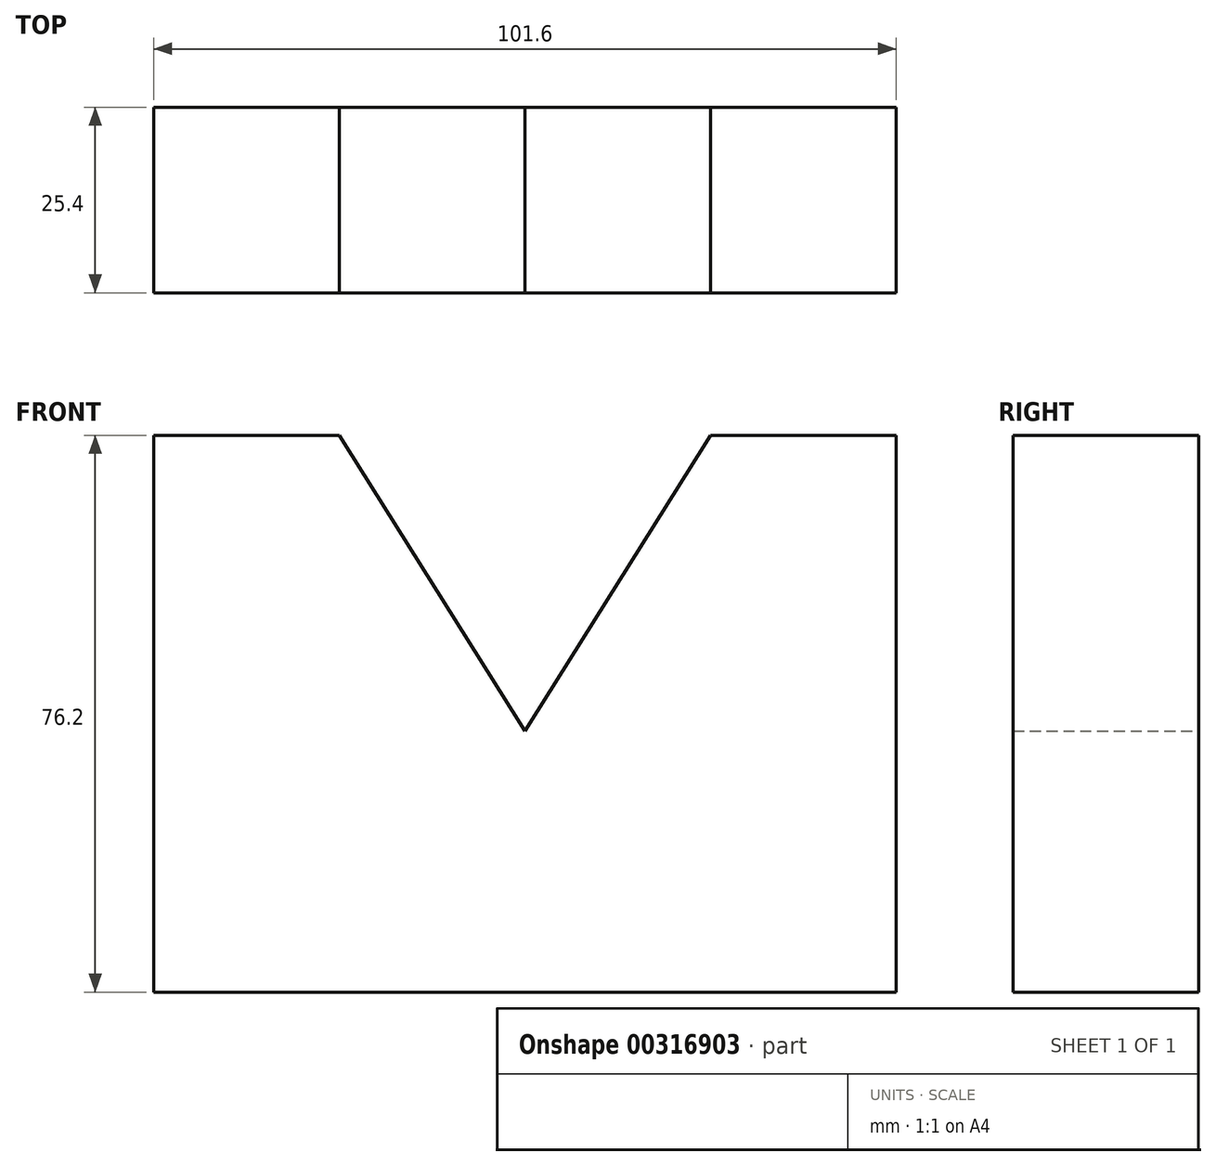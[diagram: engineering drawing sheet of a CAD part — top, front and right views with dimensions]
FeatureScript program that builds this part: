
annotation { "Feature Type Name" : "Feature", "Feature Type Description" : "" }
export const myFeature = defineFeature(function(context is Context, id is Id, definition is map)
    precondition{}
    {
        {
            var Q0;
            Q0=qCreatedBy(makeId("Front.planeOp"),FACE);
            var sketch = newSketch(context, id + "F0", { "sketchPlane" : qUnion([Q0])});
            skLineSegment(sketch, "E0", {"start": v(-47.04, 43.55) * mm, "end": v(-47.04, -32.65) * mm});
            skLineSegment(sketch, "E1", {"start": v(-47.04, -32.65) * mm, "end": v(54.56, -32.65) * mm});
            skLineSegment(sketch, "E2", {"start": v(54.56, -32.65) * mm, "end": v(54.56, 43.55) * mm});
            skLineSegment(sketch, "E3", {"start": v(54.56, 43.55) * mm, "end": v(29.16, 43.55) * mm});
            skLineSegment(sketch, "E4", {"start": v(29.16, 43.55) * mm, "end": v(3.76, 3.05) * mm});
            skLineSegment(sketch, "E5", {"start": v(3.76, 3.05) * mm, "end": v(-21.64, 43.55) * mm});
            skLineSegment(sketch, "E6", {"start": v(-47.04, 43.55) * mm, "end": v(-21.64, 43.55) * mm});
            skSolve(sketch);
        }
        {
            var Q0;
            Q0=makeQuery(id+"F0.imprint","IMPRINT",FACE,{"disambiguationData":[TD([[makeQuery(id+"F0.imprint","IMPRINT",EDGE,{"derivedFrom":sQuery(id+"F0.wireOp",EDGE,"E0")}),1.0]])]});
            extrude(context, id + "F1", {"entities" : qUnion([Q0]), "depth" : 25.4 * mm});
        }
    });
